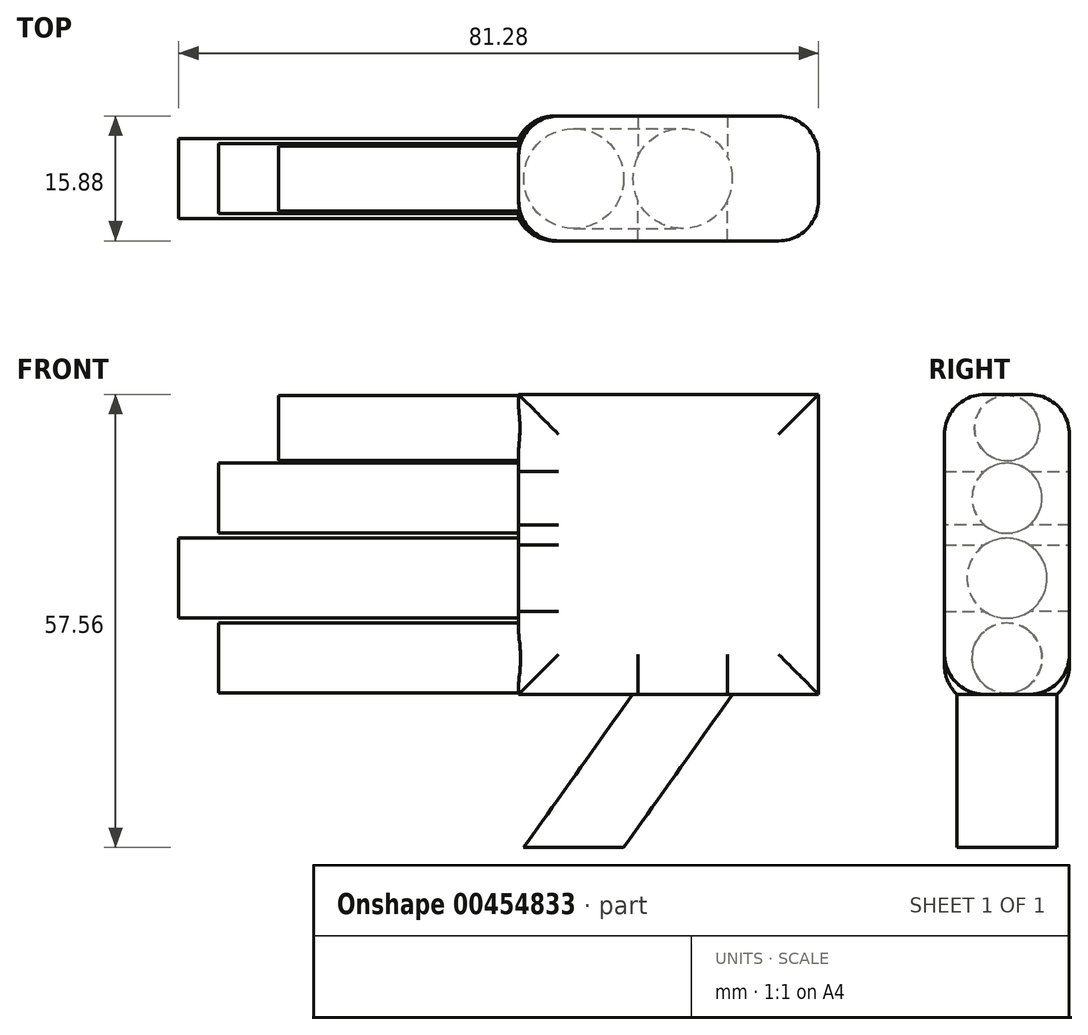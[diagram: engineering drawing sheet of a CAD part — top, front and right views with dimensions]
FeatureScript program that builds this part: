
annotation { "Feature Type Name" : "Feature", "Feature Type Description" : "" }
export const myFeature = defineFeature(function(context is Context, id is Id, definition is map)
    precondition{}
    {
        {
            var Q0;
            Q0=qCreatedBy(makeId("Front.planeOp"),FACE);
            var sketch = newSketch(context, id + "F0", { "sketchPlane" : qUnion([Q0])});
            skLineSegment(sketch, "E0.bottom", {"start": v(0, 37.98) * mm, "end": v(38.1, 37.98) * mm});
            skLineSegment(sketch, "E0.top", {"start": v(0, -0.12) * mm, "end": v(38.1, -0.12) * mm});
            skLineSegment(sketch, "E0.left", {"start": v(0, 37.98) * mm, "end": v(0, -0.12) * mm});
            skLineSegment(sketch, "E0.right", {"start": v(38.1, 37.98) * mm, "end": v(38.1, -0.12) * mm});
            skPoint(sketch, "E0.middle", {"position": v(24.13, 1.88) * mm});
            skLineSegment(sketch, "E1", {"start": v(28.8, -0.12) * mm, "end": v(14.42, -20.34) * mm});
            skLineSegment(sketch, "E2", {"start": v(0, 5.97) * mm, "end": v(-38.1, 5.97) * mm});
            skLineSegment(sketch, "E3", {"start": v(0, 14.25) * mm, "end": v(-43.18, 14.25) * mm});
            skLineSegment(sketch, "E4", {"start": v(0, 23.02) * mm, "end": v(-38.1, 23.02) * mm});
            skLineSegment(sketch, "E5", {"start": v(0, 31.3) * mm, "end": v(-30.48, 31.3) * mm});
            skPoint(sketch, "E6.startSnap0", {"position": v(-15.24, 14.25) * mm});
            skPoint(sketch, "E7.startSnap0", {"position": v(-19.05, 5.97) * mm});
            skPoint(sketch, "E8.startSnap0", {"position": v(-21.6, -2.8) * mm});
            skPoint(sketch, "E8.endSnap0", {"position": v(-21.6, -2.8) * mm});
            skPoint(sketch, "E9.startSnap0", {"position": v(-19.05, -11.08) * mm});
            skSolve(sketch);
        }
        {
            var Q0;
            {var subQ1=sQuery(id+"F0.wireOp",EDGE,"E0.bottom");Q0=makeQuery(id+"F0.imprint","IMPRINT",FACE,{"disambiguationData":[TD([[makeQuery(id+"F0.imprint","IMPRINT",EDGE,{"derivedFrom":subQ1}),-1.0]])]});}
            extrude(context, id + "F1", {"entities" : qUnion([Q0]), "endBound" : BoundingType.SYMMETRIC, "depth" : 15.88 * mm});
        }
        {
            var Q0;
            Q0=qCreatedBy(makeId("Right.planeOp"),FACE);
            var sketch = newSketch(context, id + "F2", { "sketchPlane" : qUnion([Q0])});
            skCircle(sketch, "E10", {"center": v(0, 33.7) * mm, "radius": 4.13 * mm});
            skCircle(sketch, "E11", {"center": v(0, 24.8) * mm, "radius": 4.45 * mm});
            skCircle(sketch, "E12", {"center": v(0, 14.64) * mm, "radius": 5.08 * mm});
            skCircle(sketch, "E13", {"center": v(0, 4.48) * mm, "radius": 4.45 * mm});
            skSolve(sketch);
        }
        {
            var Q0;
            Q0=makeQuery(id+"F2.imprint","IMPRINT",FACE,{"disambiguationData":[TD([[makeQuery(id+"F2.imprint","IMPRINT",EDGE,{"derivedFrom":sQuery(id+"F2.wireOp",EDGE,"E10")}),1.0]])]});
            var Q1;
            Q1=sQuery(id+"F0.wireOp",EDGE,"E5");
            sweep(context, id + "F3", {"operationType" : NewBodyOperationType.ADD, "profiles" : qUnion([Q0]), "path" : qUnion([Q1])});
        }
        {
            var Q0;
            Q0=makeQuery(id+"F2.imprint","IMPRINT",FACE,{"disambiguationData":[TD([[makeQuery(id+"F2.imprint","IMPRINT",EDGE,{"derivedFrom":sQuery(id+"F2.wireOp",EDGE,"E11")}),1.0]])]});
            var Q1;
            Q1=sQuery(id+"F0.wireOp",EDGE,"E4");
            sweep(context, id + "F4", {"operationType" : NewBodyOperationType.ADD, "profiles" : qUnion([Q0]), "path" : qUnion([Q1])});
        }
        {
            var Q0;
            Q0=makeQuery(id+"F2.imprint","IMPRINT",FACE,{"disambiguationData":[TD([[makeQuery(id+"F2.imprint","IMPRINT",EDGE,{"derivedFrom":sQuery(id+"F2.wireOp",EDGE,"E12")}),1.0]])]});
            var Q1;
            Q1=sQuery(id+"F0.wireOp",EDGE,"E3");
            sweep(context, id + "F5", {"operationType" : NewBodyOperationType.ADD, "profiles" : qUnion([Q0]), "path" : qUnion([Q1])});
        }
        {
            var Q0;
            Q0=makeQuery(id+"F2.imprint","IMPRINT",FACE,{"disambiguationData":[TD([[makeQuery(id+"F2.imprint","IMPRINT",EDGE,{"derivedFrom":sQuery(id+"F2.wireOp",EDGE,"E13")}),1.0]])]});
            var Q1;
            Q1=sQuery(id+"F0.wireOp",EDGE,"E2");
            sweep(context, id + "F6", {"operationType" : NewBodyOperationType.ADD, "profiles" : qUnion([Q0]), "path" : qUnion([Q1])});
        }
        {
            var Q0;
            Q0=qCreatedBy(makeId("Top.planeOp"),FACE);
            var sketch = newSketch(context, id + "F7", { "sketchPlane" : qUnion([Q0])});
            skCircle(sketch, "E14", {"center": v(20.91, 0) * mm, "radius": 6.35 * mm});
            skSolve(sketch);
        }
        {
            var Q0;
            Q0 = qSketchRegion(id + "F7", true);
            var Q1;
            Q1=sQuery(id+"F0.wireOp",EDGE,"E1");
            sweep(context, id + "F8", {"operationType" : NewBodyOperationType.ADD, "profiles" : qUnion([Q0]), "path" : qUnion([Q1])});
        }
        {
            var Q0;
            Q0=makeQuery(id+"F1.opExtrude","CAP_EDGE",EDGE,{"disambiguationData":[OSD([sQuery(id+"F0.wireOp",EDGE,"E0.top")])],"isStart":false});
            var Q1;
            Q1=makeQuery(id+"F1.opExtrude","CAP_EDGE",EDGE,{"disambiguationData":[OSD([sQuery(id+"F0.wireOp",EDGE,"E0.bottom")])],"isStart":false});
            var Q2;
            Q2=makeQuery(id+"F1.opExtrude","CAP_EDGE",EDGE,{"disambiguationData":[OSD([sQuery(id+"F0.wireOp",EDGE,"E0.left")])],"isStart":false});
            var Q3;
            Q3=makeQuery(id+"F1.opExtrude","CAP_EDGE",EDGE,{"disambiguationData":[OSD([sQuery(id+"F0.wireOp",EDGE,"E0.right")])],"isStart":false});
            var Q4;
            Q4=makeQuery(id+"F1.opExtrude","CAP_EDGE",EDGE,{"disambiguationData":[OSD([sQuery(id+"F0.wireOp",EDGE,"E0.bottom")])],"isStart":true});
            var Q5;
            Q5=makeQuery(id+"F1.opExtrude","CAP_EDGE",EDGE,{"disambiguationData":[OSD([sQuery(id+"F0.wireOp",EDGE,"E0.left")])],"isStart":true});
            var Q6;
            Q6=makeQuery(id+"F1.opExtrude","CAP_EDGE",EDGE,{"disambiguationData":[OSD([sQuery(id+"F0.wireOp",EDGE,"E0.right")])],"isStart":true});
            var Q7;
            Q7=makeQuery(id+"F1.opExtrude","CAP_FACE",FACE,{"disambiguationData":[OSD([sQuery(id+"F0.wireOp",EDGE,"E0.bottom"),sQuery(id+"F0.wireOp",EDGE,"E0.top"),sQuery(id+"F0.wireOp",EDGE,"E0.left"),sQuery(id+"F0.wireOp",EDGE,"E0.right")])],"isStart":true});
            fillet(context, id + "F9", {"entities" : qUnion([Q0, Q1, Q2, Q3, Q4, Q5, Q6, Q7]), "radius" : 5.08 * mm, "tangentPropagation" : true, "allowEdgeOverflow" : false});
        }
    });
